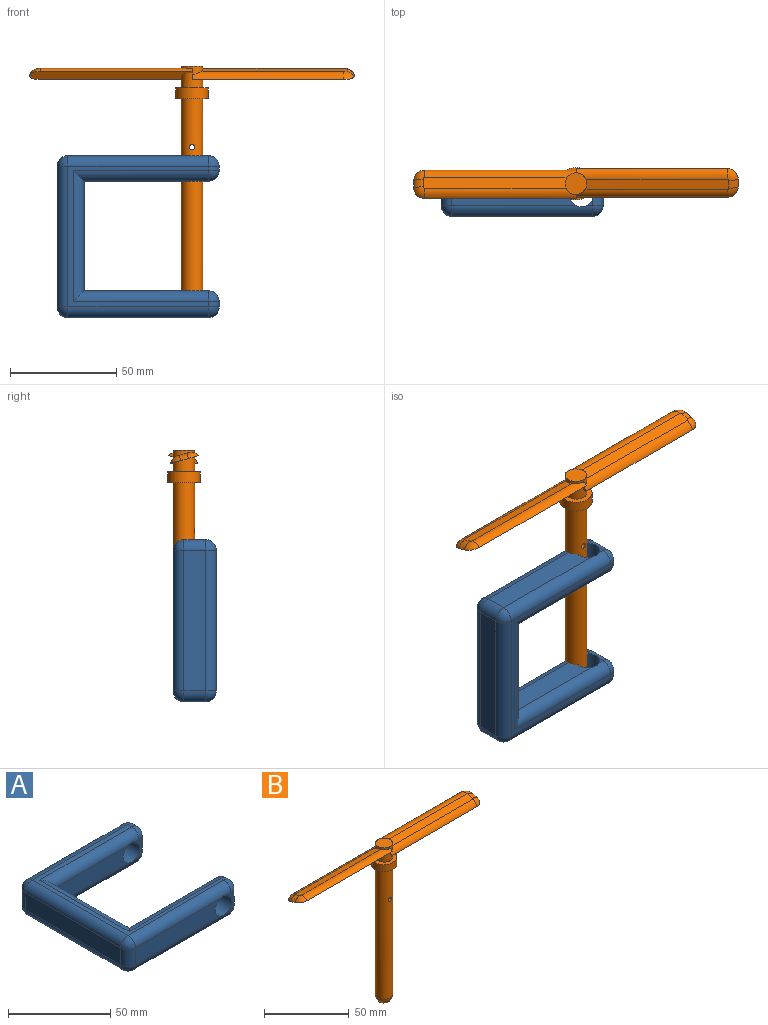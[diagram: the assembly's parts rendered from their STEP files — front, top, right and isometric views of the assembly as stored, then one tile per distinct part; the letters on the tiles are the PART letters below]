
ASSEMBLY  parts=2 mates=1
PART A: 54 faces, bbox 76.2x76.2x20.3 mm
  f0: plane 2.46x2.46mm, normal (0,-1,0), area 2.4mm2, adj f19,f41,f42
  f1: plane 2.46x2.46mm, normal (0,-1,0), area 2.4mm2, adj f19,f38,f42
  f2: plane 2.46x2.46mm, normal (0,1,0), area 2.4mm2, adj f18,f21,f22
  f3: plane 58.34x10.16mm, normal (0,1,0), area 570.3mm2, adj f18,f20,f22,f23
  f4: plane 50.72x10.16mm, normal (0,-1,0), area 492.9mm2, adj f10,f18,f39,f40
  f5: plane 2.46x2.46mm, normal (0,-1,0), area 2.4mm2, adj f18,f30,f40
  f6: plane 2.46x2.46mm, normal (0,1,0), area 2.4mm2, adj f19,f49,f53
  f7: plane 50.72x10.16mm, normal (0,1,0), area 492.9mm2, adj f10,f19,f48,f49
  f8: plane 10.16x1.85mm, normal (1,0,0), area 18.7mm2, adj f42,f47,f50,f53
  f9: plane 2.46x2.46mm, normal (0,1,0), area 2.4mm2, adj f19,f48,f53
  f10: plane 51.5x10.16mm, normal (1,0,0), area 523.2mm2, adj f4,f7,f44,f45
  f11: plane 2.46x2.46mm, normal (0,-1,0), area 2.4mm2, adj f18,f30,f39
  f12: plane 10.16x2.54mm, normal (1,0,0), area 25.8mm2, adj f21,f29,f30,f31
  f13: plane 2.46x2.46mm, normal (0,1,0), area 2.4mm2, adj f18,f20,f21
  f14: plane 66.04x10.16mm, normal (-1,0,0), area 671mm2, adj f23,f28,f32,f33
  f15: plane 58.34x10.16mm, normal (0,-1,0), area 570.3mm2, adj f19,f33,f38,f41
  f16: plane 66.04x66.04mm, normal (0,0,1), area 446.2mm2, adj f20,f28,f29,f38,f39,f44,f47,f48
  f17: plane 66.04x66.04mm, normal (0,0,-1), area 446.2mm2, adj f22,f31,f32,f40,f41,f45,f49,f50
  f18: cylinder r=5.71mm len=12.7mm, axis (0,-1,0), area 456mm2, adj f2,f3,f4,f5,f11,f13,f20,f21
  f19: cylinder r=5.71mm len=12.01mm, axis (0,-1,0), area 431.1mm2, adj f0,f1,f6,f7,f9,f15,f38,f41
  f20: cylinder r=5.08mm len=66.04mm, axis (1,0,0), area 524.7mm2, adj f3,f13,f16,f18,f24,f25
  f21: cylinder r=5.08mm len=10.16mm, axis (0,0,-1), area 78.8mm2, adj f2,f12,f13,f18,f25,f26
  f22: cylinder r=5.08mm len=66.04mm, axis (-1,0,0), area 524.7mm2, adj f2,f3,f17,f18,f26,f27
  f23: cylinder r=5.08mm len=10.16mm, axis (0,0,-1), area 81.1mm2, adj f3,f14,f24,f27
  f24: sphere r=5.08mm, area 40.5mm2, adj f20,f23,f28
  f25: sphere r=5.08mm, area 40.5mm2, adj f20,f21,f29
  f26: sphere r=5.08mm, area 40.5mm2, adj f21,f22,f31
  f27: sphere r=5.08mm, area 40.5mm2, adj f22,f23,f32
  f28: cylinder r=5.08mm len=66.04mm, axis (0,1,0), area 527mm2, adj f14,f16,f24,f34
  f29: cylinder r=5.08mm len=5.08mm, axis (0,-1,0), area 20.3mm2, adj f12,f16,f25,f35
  f30: cylinder r=5.08mm len=10.16mm, axis (0,0,-1), area 78.8mm2, adj f5,f11,f12,f18,f35,f36
  f31: cylinder r=5.08mm len=5.08mm, axis (0,1,0), area 20.3mm2, adj f12,f17,f26,f36
  f32: cylinder r=5.08mm len=66.04mm, axis (0,-1,0), area 527mm2, adj f14,f17,f27,f37
  f33: cylinder r=5.08mm len=10.16mm, axis (0,0,-1), area 81.1mm2, adj f14,f15,f34,f37
  f34: sphere r=5.08mm, area 40.5mm2, adj f28,f33,f38
  f35: sphere r=5.08mm, area 40.5mm2, adj f29,f30,f39
  f36: sphere r=5.08mm, area 40.5mm2, adj f30,f31,f40
  f37: sphere r=5.08mm, area 40.5mm2, adj f32,f33,f41
  f38: cylinder r=5.08mm len=66.04mm, axis (-1,0,0), area 524.7mm2, adj f1,f15,f16,f19,f34,f43
  f39: cylinder r=5.08mm len=63.5mm, axis (-1,0,0), area 478.7mm2, adj f4,f11,f16,f18,f35,f44
  f40: cylinder r=5.08mm len=63.5mm, axis (1,0,0), area 478.7mm2, adj f4,f5,f17,f18,f36,f45
  f41: cylinder r=5.08mm len=66.04mm, axis (1,0,0), area 524.7mm2, adj f0,f15,f17,f19,f37,f46
  f42: cylinder r=5.08mm len=10.16mm, axis (0,0,-1), area 78.8mm2, adj f0,f1,f8,f19,f43,f46
  f43: sphere r=5.08mm, area 40.5mm2, adj f38,f42,f47
  f44: cylinder r=5.08mm len=61.66mm, axis (0,-1,0), area 440.4mm2, adj f10,f16,f39,f48
  f45: cylinder r=5.08mm len=61.66mm, axis (0,1,0), area 440.4mm2, adj f10,f17,f40,f49
  f46: sphere r=5.08mm, area 40.5mm2, adj f41,f42,f50
  f47: cylinder r=5.08mm len=5.08mm, axis (0,-1,0), area 14.7mm2, adj f8,f16,f43,f51
  f48: cylinder r=5.08mm len=63.5mm, axis (1,0,0), area 478.7mm2, adj f7,f9,f16,f19,f44,f51
  f49: cylinder r=5.08mm len=63.5mm, axis (-1,0,0), area 478.7mm2, adj f6,f7,f17,f19,f45,f52
  f50: cylinder r=5.08mm len=5.08mm, axis (0,1,0), area 14.7mm2, adj f8,f17,f46,f52
  f51: sphere r=5.08mm, area 40.5mm2, adj f47,f48,f53
  f52: sphere r=5.08mm, area 40.5mm2, adj f49,f50,f53
  f53: cylinder r=5.08mm len=10.16mm, axis (0,0,-1), area 78.8mm2, adj f6,f8,f9,f19,f51,f52
PART B: 26 faces, bbox 152.4x15.3x114.3 mm
  f0: cylinder r=5.08mm len=10.16mm, axis (0,0,-1), area 248.9mm2, adj f1,f2,f3,f4,f5,f6,f7,f8
  f1: plane 10.16x10.16mm, normal (0,0,1), area 81.1mm2, adj f0
  f2: plane 2.29x1.27mm, normal (-1,0,0), area 1.5mm2, adj f0,f4,f14
  f3: plane 1.97x1.74mm, normal (-1,0,0), area 1.9mm2, adj f0,f4,f10
  f4: plane 76.2x13.4mm, normal (0,0.27,-0.96), area 1008mm2, adj f0,f2,f3,f10,f11,f12,f13,f14
  f5: plane 67.61x4.97mm, normal (0,-0.27,0.96), area 343mm2, adj f0,f10,f11,f12,f13,f14
  f6: plane 2.29x1.27mm, normal (1,0,0), area 1.5mm2, adj f0,f8,f19
  f7: plane 1.97x1.74mm, normal (1,0,0), area 1.9mm2, adj f0,f8,f15
  f8: plane 76.2x13.4mm, normal (0,-0.27,-0.96), area 1008mm2, adj f0,f6,f7,f15,f16,f17,f18,f19
  f9: plane 67.62x4.98mm, normal (0,0.27,0.96), area 343mm2, adj f0,f15,f16,f17,f18,f19
  f10: cylinder r=5.08mm len=71.12mm, axis (-1,0,0), area 368.4mm2, adj f0,f3,f4,f5,f11
  f11: torus R=0.68mm, axis (0,-0.27,0.96), area 26mm2, adj f4,f5,f10,f12
  f12: cylinder r=5.08mm len=4.4mm, axis (0,-0.96,-0.27), area 20mm2, adj f4,f5,f11,f13
  f13: torus R=0.68mm, axis (0,-0.27,0.96), area 26mm2, adj f4,f5,f12,f14
  f14: cylinder r=5.08mm len=71.12mm, axis (1,0,0), area 370.6mm2, adj f0,f2,f4,f5,f13
  f15: cylinder r=5.08mm len=71.12mm, axis (1,0,0), area 368.4mm2, adj f0,f7,f8,f9,f16
  f16: torus R=0.68mm, axis (0,0.27,0.96), area 26mm2, adj f8,f9,f15,f17
  f17: cylinder r=5.08mm len=4.4mm, axis (0,0.96,-0.27), area 20mm2, adj f8,f9,f16,f18
  f18: torus R=0.68mm, axis (0,0.27,0.96), area 26mm2, adj f8,f9,f17,f19
  f19: cylinder r=5.08mm len=71.12mm, axis (-1,0,0), area 370.6mm2, adj f0,f6,f8,f9,f18
  f20: cylinder r=7.62mm len=15.24mm, axis (0,0,1), area 243.2mm2, adj f21,f22
  f21: plane 15.24x15.24mm, normal (0,0,-1), area 101.3mm2, adj f20,f25
  f22: plane 15.24x15.24mm, normal (0,0,1), area 101.3mm2, adj f0,f20
  f23: cylinder r=1.27mm len=10.16mm, axis (0,-1,0), area 79.8mm2, adj f25
  f24: sphere r=5.08mm, area 162.1mm2, adj f25
  f25: cylinder r=5.08mm len=93.98mm, axis (0,0,-1), area 2989.5mm2, adj f21,f23,f24
PLACE A rot(axis=(-1,0,0),90deg) t=(40.09,-8.35,25.98)mm fixed
PLACE B t=(27.32,6.89,-8.18)mm
MATE slider A.f7 <-> B.f0  axis (0,0,-1) through (27.32,6.89,13.97)mm
